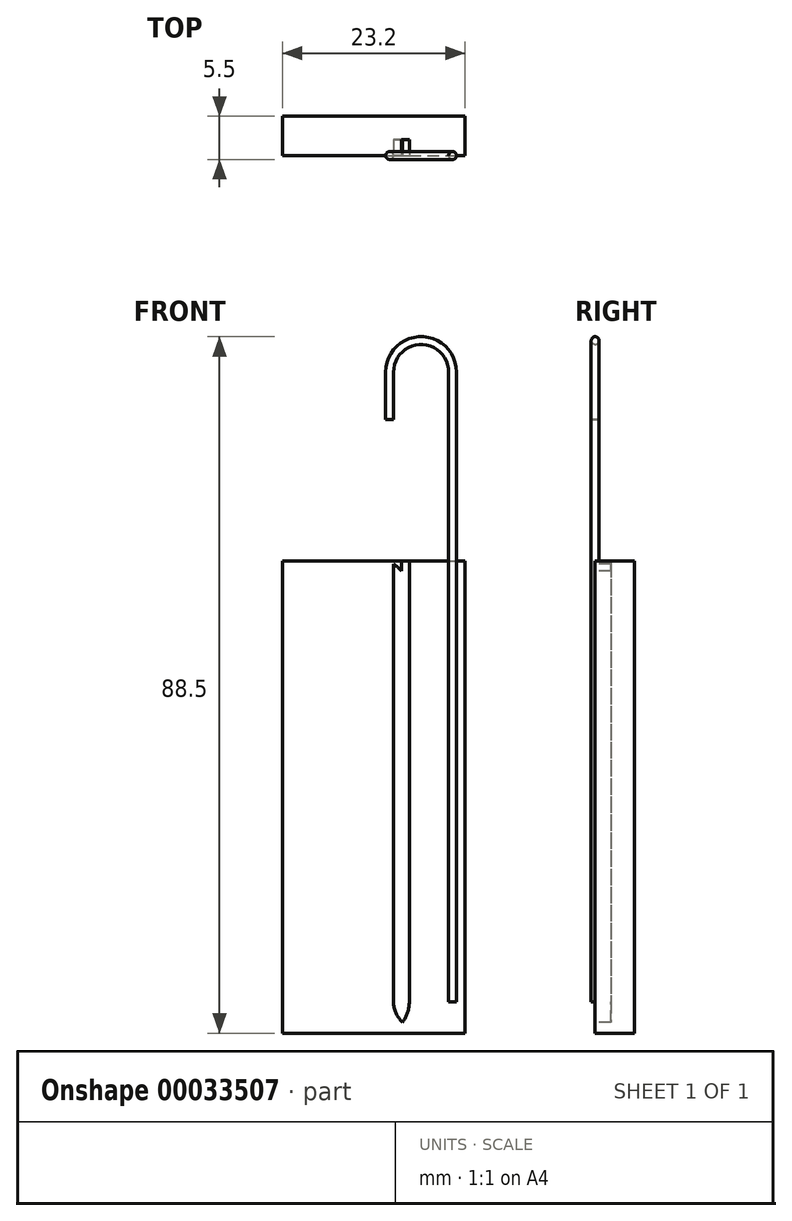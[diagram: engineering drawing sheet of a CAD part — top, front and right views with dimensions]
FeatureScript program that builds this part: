
annotation { "Feature Type Name" : "Feature", "Feature Type Description" : "" }
export const myFeature = defineFeature(function(context is Context, id is Id, definition is map)
    precondition{}
    {
        {
            var Q0;
            Q0=qCreatedBy(makeId("Front.planeOp"),FACE);
            var sketch = newSketch(context, id + "F0", { "sketchPlane" : qUnion([Q0])});
            skLineSegment(sketch, "E0.rect.bottom", {"start": v(10, -40) * mm, "end": v(2, -40) * mm, "construction": true});
            skLineSegment(sketch, "E0.rect.top", {"start": v(10, 40) * mm, "end": v(2, 40) * mm, "construction": true});
            skLineSegment(sketch, "E0.rect.left", {"start": v(10, -40) * mm, "end": v(10, 40) * mm});
            skLineSegment(sketch, "E0.rect.right", {"start": v(2, -40) * mm, "end": v(2, 15.4) * mm});
            skPoint(sketch, "E0.rect.middle", {"position": v(50, 0) * mm});
            skArc(sketch, "E1", {"start": v(10, 40) * mm, "mid": v(6, 44) * mm, "end": v(2, 40) * mm});
            skArc(sketch, "E2", {"start": v(2, -40) * mm, "mid": v(6, -44) * mm, "end": v(10, -40) * mm});
            skArc(sketch, "E3", {"start": v(10, 5.6) * mm, "mid": v(7.75, 11.93) * mm, "end": v(2, 15.4) * mm, "construction": true});
            skPoint(sketch, "E4", {"position": v(2, 34) * mm});
            skLineSegment(sketch, "E5.trimOffspring", {"start": v(2, 34) * mm, "end": v(2, 40) * mm});
            skSolve(sketch);
        }
        {
            var Q0;
            Q0=qCreatedBy(makeId("Front.planeOp"),FACE);
            var sketch = newSketch(context, id + "F1", { "sketchPlane" : qUnion([Q0])});
            skLineSegment(sketch, "E6.rect.bottom", {"start": v(-11.6, 16) * mm, "end": v(11.6, 16) * mm});
            skLineSegment(sketch, "E6.rect.top", {"start": v(-11.6, -44) * mm, "end": v(11.6, -44) * mm});
            skLineSegment(sketch, "E6.rect.left", {"start": v(-11.6, 16) * mm, "end": v(-11.6, -44) * mm});
            skLineSegment(sketch, "E6.rect.right", {"start": v(11.6, 16) * mm, "end": v(11.6, -44) * mm});
            skPoint(sketch, "E6.rect.middle", {"position": v(0, -14) * mm});
            skSolve(sketch);
        }
        {
            var Q0;
            Q0=makeQuery(id+"F1.imprint","IMPRINT",FACE,{"disambiguationData":[TD([[makeQuery(id+"F1.imprint","IMPRINT",EDGE,{"derivedFrom":sQuery(id+"F1.wireOp",EDGE,"E6.rect.bottom")}),-1.0]])]});
            extrude(context, id + "F2", {"entities" : qUnion([Q0]), "oppositeDirection" : true, "depth" : 5 * mm});
        }
        {
            var Q0;
            Q0=makeQuery(id+"F1.imprint","IMPRINT",FACE,{"disambiguationData":[TD([[makeQuery(id+"F1.imprint","IMPRINT",EDGE,{"derivedFrom":sQuery(id+"F1.wireOp",EDGE,"E6.rect.bottom")}),-1.0]])]});
            var sketch = newSketch(context, id + "F3", { "sketchPlane" : qUnion([Q0])});
            skSolve(sketch);
        }
        {
            var Q0;
            Q0=makeQuery(id+"F3.imprint","IMPRINT",FACE,{"disambiguationData":[TD([[makeQuery(id+"F3.imprint","IMPRINT",EDGE,{"derivedFrom":makeQuery(id+"F1.imprint","IMPRINT",EDGE,{"derivedFrom":sQuery(id+"F1.wireOp",EDGE,"E6.rect.bottom")})}),-1.0]])]});
            var sketch = newSketch(context, id + "F4", { "sketchPlane" : qUnion([Q0])});
            skLineSegment(sketch, "E7", {"start": v(2, 15.4) * mm, "end": v(2, -40) * mm, "construction": true});
            skLineSegment(sketch, "E8", {"start": v(10, 5.6) * mm, "end": v(10, -40) * mm, "construction": true});
            skArc(sketch, "E9", {"start": v(2, -40) * mm, "mid": v(6, -44) * mm, "end": v(10, -40) * mm, "construction": true});
            skArc(sketch, "E10", {"start": v(10, 5.6) * mm, "mid": v(19.75, 21.73) * mm, "end": v(2, 15.4) * mm, "construction": true});
            skLineSegment(sketch, "E11", {"start": v(10, 5.6) * mm, "end": v(10, 40) * mm, "construction": true});
            skLineSegment(sketch, "E12", {"start": v(2, 40) * mm, "end": v(2, 34) * mm, "construction": true});
            skArc(sketch, "E13", {"start": v(10, 40) * mm, "mid": v(6, 44) * mm, "end": v(2, 40) * mm, "construction": true});
            skLineSegment(sketch, "E14.1", {"start": v(4.5, 12.02) * mm, "end": v(4.5, -39.98) * mm});
            skArc(sketch, "E14.2", {"start": v(-4.5, -39.97) * mm, "mid": v(-3.82, -42.34) * mm, "end": v(-2, -44) * mm});
            skLineSegment(sketch, "E14.3", {"start": v(-4.5, 11.89) * mm, "end": v(-4.5, -39.97) * mm});
            skArc(sketch, "E15.0", {"start": v(9.5, 6.24) * mm, "mid": v(19.55, 21.17) * mm, "end": v(2.5, 15.4) * mm});
            skLineSegment(sketch, "E15.1", {"start": v(9.5, 6.24) * mm, "end": v(9.5, -40) * mm});
            skArc(sketch, "E15.2", {"start": v(2.5, -40) * mm, "mid": v(6, -43.5) * mm, "end": v(9.5, -40) * mm});
            skLineSegment(sketch, "E15.3", {"start": v(2.5, 15.4) * mm, "end": v(2.5, -40) * mm});
            skLineSegment(sketch, "E16", {"start": v(4.5, 12.02) * mm, "end": v(4.5, 16) * mm});
            skArc(sketch, "E17.trimOffspring", {"start": v(3.5, 14.72) * mm, "mid": v(2.74, 15.46) * mm, "end": v(1.83, 16) * mm});
            skLineSegment(sketch, "E18", {"start": v(3.5, 16) * mm, "end": v(4.5, 16) * mm});
            skLineSegment(sketch, "E19", {"start": v(-1.83, 16) * mm, "end": v(1.83, 16) * mm});
            skArc(sketch, "E20.trimOffspring", {"start": v(-1.83, 16) * mm, "mid": v(-3.77, 14.34) * mm, "end": v(-4.5, 11.89) * mm});
            skLineSegment(sketch, "E21", {"start": v(-2, -44) * mm, "end": v(2.01, -44) * mm});
            skArc(sketch, "E22.trimOffspring", {"start": v(2.01, -44) * mm, "mid": v(3.83, -42.34) * mm, "end": v(4.5, -39.98) * mm});
            skLineSegment(sketch, "E23.trimOffspring", {"start": v(3.5, 14.72) * mm, "end": v(3.5, 16) * mm});
            skSolve(sketch);
        }
        {
            var Q0;
            Q0=makeQuery(id+"F4.imprint","IMPRINT",FACE,{"disambiguationData":[TD([[makeQuery(id+"F4.imprint","IMPRINT",EDGE,{"derivedFrom":sQuery(id+"F4.wireOp",EDGE,"E14.1")}),-1.0]])]});
            extrude(context, id + "F5", {"entities" : qUnion([Q0]), "operationType" : NewBodyOperationType.REMOVE, "oppositeDirection" : true, "depth" : 2 * mm});
        }
        {
            var Q0;
            Q0=qCreatedBy(makeId("Top.planeOp"),FACE);
            var Q1;
            Q1=sQuery(id+"F0.wireOp",VERTEX,"E4");
            cPlane(context, id + "F6", {"entities" : qUnion([Q0, Q1]), "cplaneType" : CPlaneType.PLANE_POINT, "offset" : 150 * mm, "width" : 150 * mm, "height" : 150 * mm});
        }
        {
            var Q0;
            Q0=qCreatedBy(id+"F6.planeOp",FACE);
            var sketch = newSketch(context, id + "F7", { "sketchPlane" : qUnion([Q0])});
            skCircle(sketch, "E24", {"center": v(2, 0) * mm, "radius": 0.5 * mm});
            skSolve(sketch);
        }
        {
            var Q0;
            Q0=makeQuery(id+"F7.imprint","IMPRINT",FACE,{"disambiguationData":[TD([[makeQuery(id+"F7.imprint","IMPRINT",EDGE,{"derivedFrom":sQuery(id+"F7.wireOp",EDGE,"E24")}),1.0]])]});
            var Q1;
            Q1=sQuery(id+"F0.wireOp",EDGE,"E5.trimOffspring");
            var Q2;
            Q2=sQuery(id+"F0.wireOp",EDGE,"E1");
            var Q3;
            Q3=sQuery(id+"F0.wireOp",EDGE,"E0.rect.left");
            sweep(context, id + "F8", {"operationType" : NewBodyOperationType.ADD, "profiles" : qUnion([Q0]), "path" : qUnion([Q1, Q2, Q3])});
        }
    });
